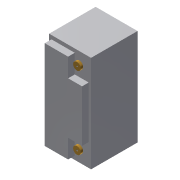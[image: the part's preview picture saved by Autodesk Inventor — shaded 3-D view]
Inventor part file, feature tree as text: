
AUTODESK INVENTOR PART (.ipt)
format: ipt  version: 2016 SP2 (Build 200236200, 236)  size: 138,752 bytes
history: native  units: mm
features: sketch x4, extrude x3, projected_geometry x2, hole x1
ambient origin geometry x8: Origin, YZ Plane, XZ Plane, XY Plane, X Axis, Y Axis, Z Axis, Center Point
bodies: Body1 (feature_tree)
feature tree (10):
  extrude  "Extrusion3"  Depth=179.0mm
  extrude  "Extrusion4"  Depth=220.0mm
  extrude  "Extrusion5"  Depth=10.0mm
  hole  "Hole1"  [1 undecoded]
  sketch  "Sketch1"  dims[d4=227.0mm d5=179.0mm]
  sketch  "Sketch2"  dims[d6=412.0mm d7=0.0mm d8=220.0mm]
  projected_geometry  "Projected Loop1"
  sketch  "Sketch3"  dims[d9=380.0mm d10=10.0mm]
  sketch  "Sketch4"  dims[d11=10.0mm d12=20.0mm d13=28.5mm d14=0.0mm d15=10.5mm d16=0.0mm d17=311.0mm d18=50.5mm d20=50.5mm d21=39.6mm d22=6.647mm d23=7.0mm d24=4.0mm d25=2.0mm d26=90.0deg d27=10.0mm d28=20.594885mm]
  projected_geometry  "Projected Loop2"
note: 1 required parameter value undecoded (feature->parameter linkage not recoverable at this tier; creation-order binding heuristic only, values carry confidence <= 0.55)
